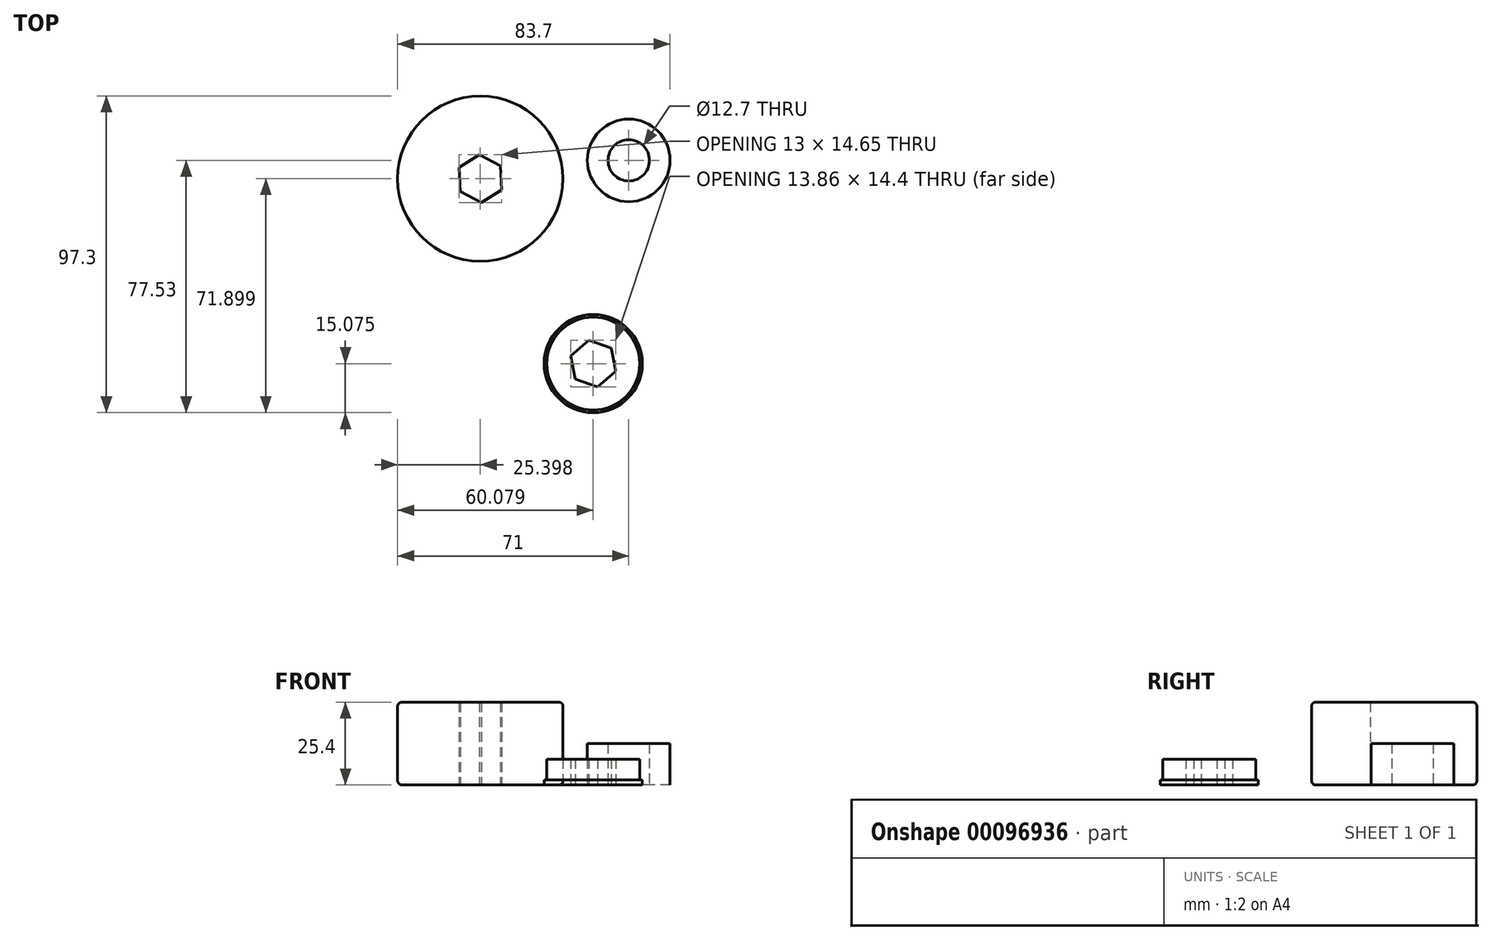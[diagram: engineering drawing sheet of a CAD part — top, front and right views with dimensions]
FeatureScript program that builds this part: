
annotation { "Feature Type Name" : "Feature", "Feature Type Description" : "" }
export const myFeature = defineFeature(function(context is Context, id is Id, definition is map)
    precondition{}
    {
        {
            var Q0;
            Q0=qCreatedBy(makeId("Top.planeOp"),FACE);
            var sketch = newSketch(context, id + "F0", { "sketchPlane" : qUnion([Q0])});
            skCircle(sketch, "E0", {"center": v(0, 0) * mm, "radius": 12.7 * mm});
            skCircle(sketch, "E1", {"center": v(0, 0) * mm, "radius": 6.35 * mm});
            skSolve(sketch);
        }
        {
            var Q0;
            Q0=makeQuery(id+"F0.imprint","IMPRINT",FACE,{"disambiguationData":[TD([[makeQuery(id+"F0.imprint","IMPRINT",EDGE,{"derivedFrom":sQuery(id+"F0.wireOp",EDGE,"E0")}),1.0]])]});
            extrude(context, id + "F1", {"entities" : qUnion([Q0]), "depth" : 12.7 * mm});
        }
        {
            var Q0;
            Q0=qCreatedBy(makeId("Top.planeOp"),FACE);
            var sketch = newSketch(context, id + "F2", { "sketchPlane" : qUnion([Q0])});
            skCircle(sketch, "E2.cCircle", {"center": v(-45.6, -5.63) * mm, "radius": 6.35 * mm, "construction": true});
            skLineSegment(sketch, "E2.0", {"start": v(-45.92, 1.7) * mm, "end": v(-39.42, -1.7) * mm});
            skLineSegment(sketch, "E2.1", {"start": v(-39.42, -1.7) * mm, "end": v(-39.1, -9.02) * mm});
            skLineSegment(sketch, "E2.2", {"start": v(-39.1, -9.02) * mm, "end": v(-45.29, -12.96) * mm});
            skLineSegment(sketch, "E2.3", {"start": v(-45.29, -12.96) * mm, "end": v(-51.79, -9.57) * mm});
            skLineSegment(sketch, "E2.4", {"start": v(-51.79, -9.57) * mm, "end": v(-52.1, -2.24) * mm});
            skLineSegment(sketch, "E2.5", {"start": v(-52.1, -2.24) * mm, "end": v(-45.92, 1.7) * mm});
            skPoint(sketch, "E2.0.midPoint", {"position": v(-42.67, 0) * mm});
            skCircle(sketch, "E3", {"center": v(-45.6, -5.63) * mm, "radius": 25.4 * mm});
            skSolve(sketch);
        }
        {
            var Q0;
            Q0=makeQuery(id+"F2.imprint","IMPRINT",FACE,{"disambiguationData":[TD([[makeQuery(id+"F2.imprint","IMPRINT",EDGE,{"derivedFrom":sQuery(id+"F2.wireOp",EDGE,"E2.0")}),1.0]])]});
            extrude(context, id + "F3", {"entities" : qUnion([Q0]), "depth" : 25.4 * mm});
        }
        {
            var Q0;
            Q0=makeQuery(id+"F3.opExtrude","CAP_EDGE",EDGE,{"disambiguationData":[OSD([sQuery(id+"F2.wireOp",EDGE,"E3")])],"isStart":false});
            var Q1;
            Q1=makeQuery(id+"F3.opExtrude","CAP_EDGE",EDGE,{"disambiguationData":[OSD([sQuery(id+"F2.wireOp",EDGE,"E3")])],"isStart":true});
            fillet(context, id + "F4", {"entities" : qUnion([Q0, Q1]), "radius" : 1.27 * mm, "tangentPropagation" : true, "allowEdgeOverflow" : false});
        }
        {
            var Q0;
            Q0=qCreatedBy(makeId("Top.planeOp"),FACE);
            var sketch = newSketch(context, id + "F5", { "sketchPlane" : qUnion([Q0])});
            skCircle(sketch, "E4.cCircle", {"center": v(-10.92, -62.46) * mm, "radius": 6.35 * mm, "construction": true});
            skLineSegment(sketch, "E4.0", {"start": v(-12.31, -55.26) * mm, "end": v(-5.38, -57.65) * mm});
            skLineSegment(sketch, "E4.1", {"start": v(-5.38, -57.65) * mm, "end": v(-4, -64.85) * mm});
            skLineSegment(sketch, "E4.2", {"start": v(-4, -64.85) * mm, "end": v(-9.53, -69.65) * mm});
            skLineSegment(sketch, "E4.3", {"start": v(-9.53, -69.65) * mm, "end": v(-16.46, -67.26) * mm});
            skLineSegment(sketch, "E4.4", {"start": v(-16.46, -67.26) * mm, "end": v(-17.85, -60.06) * mm});
            skLineSegment(sketch, "E4.5", {"start": v(-17.85, -60.06) * mm, "end": v(-12.31, -55.26) * mm});
            skPoint(sketch, "E4.0.midPoint", {"position": v(-8.85, -56.45) * mm});
            skCircle(sketch, "E5", {"center": v(-10.92, -62.46) * mm, "radius": 14.29 * mm});
            skCircle(sketch, "E6", {"center": v(-10.92, -62.46) * mm, "radius": 15.07 * mm});
            skSolve(sketch);
        }
        {
            var Q0;
            Q0=makeQuery(id+"F5.imprint","IMPRINT",FACE,{"disambiguationData":[TD([[makeQuery(id+"F5.imprint","IMPRINT",EDGE,{"derivedFrom":sQuery(id+"F5.wireOp",EDGE,"E4.0")}),1.0]])]});
            extrude(context, id + "F6", {"entities" : qUnion([Q0]), "depth" : 7.92 * mm});
        }
        {
            var Q0;
            Q0=makeQuery(id+"F5.imprint","IMPRINT",FACE,{"disambiguationData":[TD([[makeQuery(id+"F5.imprint","IMPRINT",EDGE,{"derivedFrom":sQuery(id+"F5.wireOp",EDGE,"E5")}),-1.0]])]});
            extrude(context, id + "F7", {"entities" : qUnion([Q0]), "operationType" : NewBodyOperationType.ADD, "depth" : 1.57 * mm});
        }
    });
